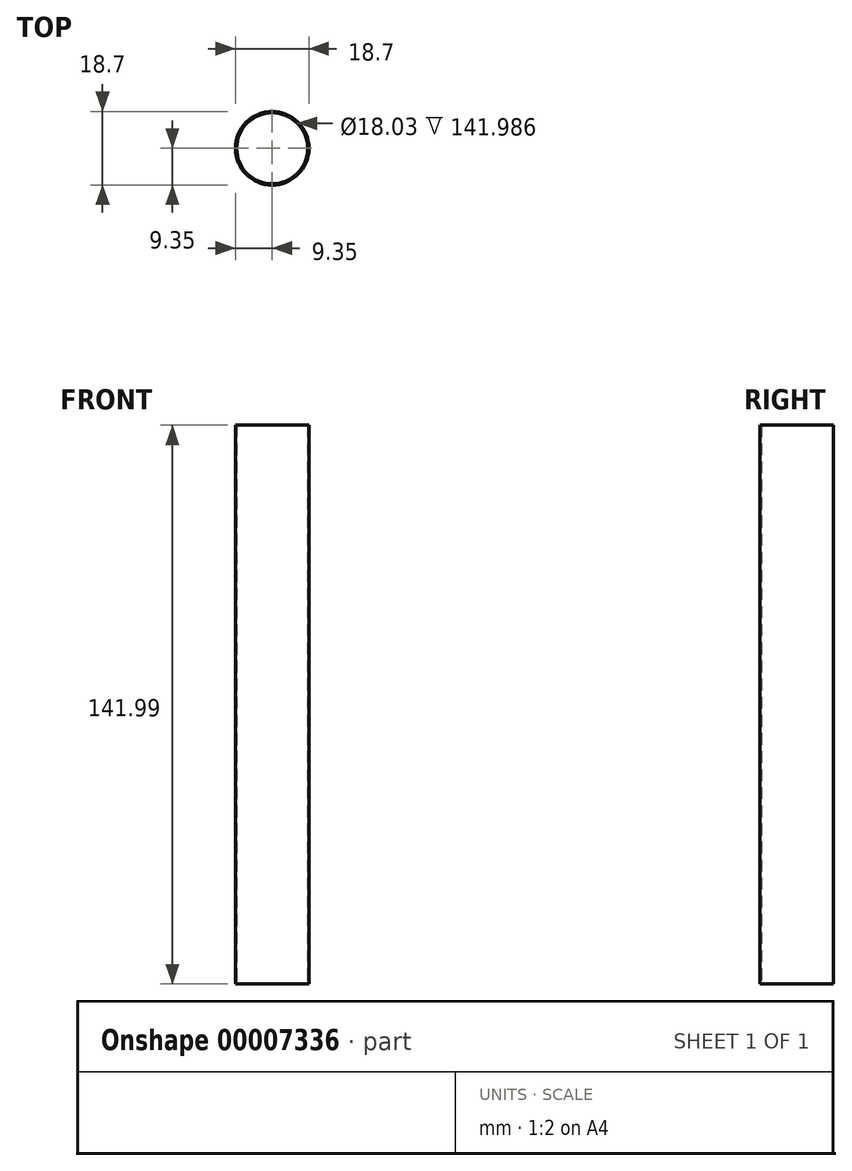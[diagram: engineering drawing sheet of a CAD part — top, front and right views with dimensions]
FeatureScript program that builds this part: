
annotation { "Feature Type Name" : "Feature", "Feature Type Description" : "" }
export const myFeature = defineFeature(function(context is Context, id is Id, definition is map)
    precondition{}
    {
        {
            var Q0;
            Q0=qCreatedBy(makeId("Front.planeOp"),FACE);
            var sketch = newSketch(context, id + "F0", { "sketchPlane" : qUnion([Q0])});
            skLineSegment(sketch, "E0.bottom", {"start": v(9.02, 0) * mm, "end": v(9.35, 0) * mm});
            skLineSegment(sketch, "E0.top", {"start": v(9.02, 141.99) * mm, "end": v(9.35, 141.99) * mm});
            skLineSegment(sketch, "E0.left", {"start": v(9.02, 0) * mm, "end": v(9.02, 141.99) * mm});
            skLineSegment(sketch, "E0.right", {"start": v(9.35, 0) * mm, "end": v(9.35, 141.99) * mm});
            skLineSegment(sketch, "E1", {"start": v(9.02, 0) * mm, "end": v(0, 0) * mm});
            skLineSegment(sketch, "E2", {"start": v(0, 0) * mm, "end": v(0, 141.99) * mm});
            skSolve(sketch);
        }
        {
            var Q0;
            Q0 = qSketchRegion(id + "F0", true);
            var Q1;
            Q1=sQuery(id+"F0.wireOp",EDGE,"E2");
            revolve(context, id + "F1", {"entities" : qUnion([Q0]), "axis" : qUnion([Q1]), "revolveType" : RevolveType.FULL});
        }
        {
            var Q0;
            Q0=qCreatedBy(makeId("Top.planeOp"),FACE);
            var sketch = newSketch(context, id + "F2", { "sketchPlane" : qUnion([Q0])});
            skCircle(sketch, "E3.0", {"center": v(0, 0) * mm, "radius": 9.35 * mm});
            skCircle(sketch, "E4", {"center": v(0, 0) * mm, "radius": 63.5 * mm});
            skLineSegment(sketch, "E5", {"start": v(0, 0) * mm, "end": v(0, 63.5) * mm});
            skLineSegment(sketch, "E6", {"start": v(0, 0) * mm, "end": v(63.5, 0) * mm});
            skLineSegment(sketch, "E7", {"start": v(0, 0) * mm, "end": v(-63.5, 0) * mm});
            skLineSegment(sketch, "E8", {"start": v(0, 0) * mm, "end": v(0, -63.5) * mm});
            skLineSegment(sketch, "E9", {"start": v(0, 0) * mm, "end": v(44.9, 44.9) * mm});
            skLineSegment(sketch, "E10", {"start": v(0, 0) * mm, "end": v(55, -31.75) * mm});
            skLineSegment(sketch, "E11.0.MirrorCS", {"start": v(0, 0) * mm, "end": v(-55, -31.75) * mm});
            skLineSegment(sketch, "E12", {"start": v(0, 0) * mm, "end": v(60.4, 19.62) * mm});
            skLineSegment(sketch, "E13", {"start": v(0, 0) * mm, "end": v(37.32, -51.37) * mm});
            skLineSegment(sketch, "E14.0.MirrorCS", {"start": v(0, 0) * mm, "end": v(-60.4, 19.62) * mm});
            skLineSegment(sketch, "E15.0.MirrorCS", {"start": v(0, 0) * mm, "end": v(-37.32, -51.37) * mm});
            skPoint(sketch, "E16", {"position": v(0, -9.35) * mm});
            skPoint(sketch, "E17", {"position": v(5.5, -7.56) * mm});
            skPoint(sketch, "E18", {"position": v(8.1, -4.67) * mm});
            skPoint(sketch, "E19", {"position": v(9.35, 0) * mm});
            skPoint(sketch, "E20", {"position": v(8.89, 2.89) * mm});
            skPoint(sketch, "E21", {"position": v(-5.5, -7.56) * mm});
            skPoint(sketch, "E22", {"position": v(-8.1, -4.67) * mm});
            skPoint(sketch, "E23", {"position": v(-9.35, 0) * mm});
            skPoint(sketch, "E24", {"position": v(-8.89, 2.89) * mm});
            skPoint(sketch, "E25", {"position": v(0, 9.35) * mm});
            skPoint(sketch, "E26", {"position": v(6.6, 6.6) * mm});
            skSolve(sketch);
        }
        {
            var Q0;
            Q0=qCreatedBy(makeId("Top.planeOp"),FACE);
            var sketch = newSketch(context, id + "F3", { "sketchPlane" : qUnion([Q0])});
            skLineSegment(sketch, "E27.0", {"start": v(0, 0) * mm, "end": v(-55, -31.75) * mm});
            skCircle(sketch, "E28.0", {"center": v(0, 0) * mm, "radius": 63.5 * mm});
            skLineSegment(sketch, "E29", {"start": v(0, 0) * mm, "end": v(-0.28, 0.49) * mm});
            skLineSegment(sketch, "E30", {"start": v(-0.28, 0.49) * mm, "end": v(-55.27, -31.26) * mm});
            skLineSegment(sketch, "E31.0.MirrorCS", {"start": v(0.28, -0.49) * mm, "end": v(-54.7, -32.24) * mm});
            skLineSegment(sketch, "E32.0.MirrorCS", {"start": v(0, 0) * mm, "end": v(0.28, -0.49) * mm});
            skCircle(sketch, "E33.0", {"center": v(0, 0) * mm, "radius": 9.35 * mm});
            skCircle(sketch, "E34", {"center": v(-8.32, -7.96) * mm, "radius": 2.17 * mm});
            skSolve(sketch);
        }
        {
            var Q0;
            Q0=qCreatedBy(makeId("Origin.pointOp"),VERTEX);
            var Q1;
            Q1=sQuery(id+"F0.wireOp",VERTEX,"E2.end");
            var Q2;
            Q2=sQuery(id+"F3.wireOp",VERTEX,"E34.center");
            cPlane(context, id + "F4", {"entities" : qUnion([Q0, Q1, Q2]), "cplaneType" : CPlaneType.THREE_POINT, "offset" : 152.4 * mm, "width" : 152.4 * mm, "height" : 152.4 * mm});
        }
        {
            var Q0;
            Q0=qCreatedBy(id+"F4.planeOp",FACE);
            var sketch = newSketch(context, id + "F5", { "sketchPlane" : qUnion([Q0])});
            skLineSegment(sketch, "E35.0", {"start": v(0, 0) * mm, "end": v(0, 141.99) * mm});
            skLineSegment(sketch, "E36", {"start": v(0, 0) * mm, "end": v(11.52, 0) * mm});
            skLineSegment(sketch, "E37", {"start": v(11.52, 0) * mm, "end": v(11.52, 141.99) * mm});
            skLineSegment(sketch, "E38", {"start": v(11.52, 141.99) * mm, "end": v(0, 141.99) * mm});
            skSolve(sketch);
        }
    });
